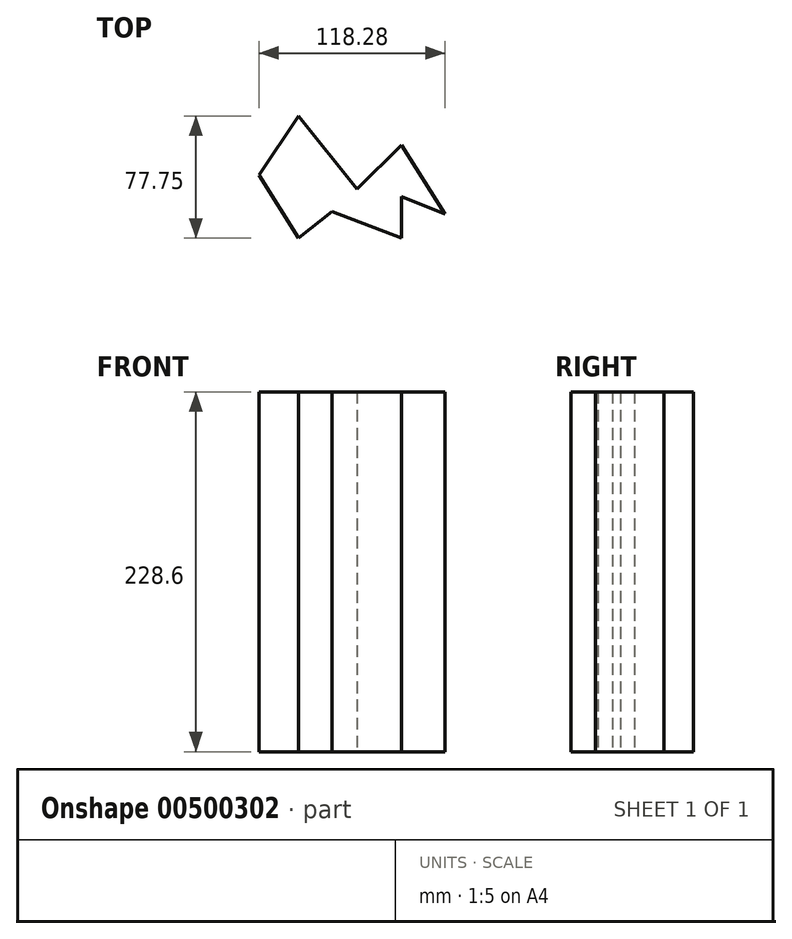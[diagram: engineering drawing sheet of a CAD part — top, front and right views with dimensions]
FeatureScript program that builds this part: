
annotation { "Feature Type Name" : "Feature", "Feature Type Description" : "" }
export const myFeature = defineFeature(function(context is Context, id is Id, definition is map)
    precondition{}
    {
        {
            var Q0;
            Q0=qCreatedBy(makeId("Top.planeOp"),FACE);
            var sketch = newSketch(context, id + "F0", { "sketchPlane" : qUnion([Q0])});
            skLineSegment(sketch, "E0", {"start": v(0, 0) * mm, "end": v(-37.2, 46.47) * mm});
            skLineSegment(sketch, "E1", {"start": v(-37.2, 46.47) * mm, "end": v(-62.5, 8.9) * mm});
            skLineSegment(sketch, "E2", {"start": v(-62.5, 8.9) * mm, "end": v(-37.2, -31.28) * mm});
            skLineSegment(sketch, "E3", {"start": v(-37.2, -31.28) * mm, "end": v(-16, -14.17) * mm});
            skLineSegment(sketch, "E4", {"start": v(0, 0) * mm, "end": v(28.27, 27.87) * mm});
            skLineSegment(sketch, "E5", {"start": v(28.27, 27.87) * mm, "end": v(55.79, -15.84) * mm});
            skLineSegment(sketch, "E6", {"start": v(55.79, -15.84) * mm, "end": v(28.27, -4.87) * mm});
            skLineSegment(sketch, "E7", {"start": v(-16, -14.17) * mm, "end": v(28.27, -31.28) * mm});
            skLineSegment(sketch, "E8", {"start": v(28.27, -4.87) * mm, "end": v(28.27, -31.28) * mm});
            skSolve(sketch);
        }
        {
            var Q0;
            Q0=qCreatedBy(makeId("Top.planeOp"),FACE);
            cPlane(context, id + "F1", {"entities" : qUnion([Q0]), "cplaneType" : CPlaneType.OFFSET, "offset" : 235.97 * mm, "width" : 152.4 * mm, "height" : 152.4 * mm});
        }
        {
            var Q0;
            Q0=makeQuery(id+"F0.imprint","IMPRINT",FACE,{"disambiguationData":[TD([[makeQuery(id+"F0.imprint","IMPRINT",EDGE,{"derivedFrom":sQuery(id+"F0.wireOp",EDGE,"E0")}),1.0]])]});
            extrude(context, id + "F2", {"entities" : qUnion([Q0]), "depth" : 228.6 * mm});
        }
    });
